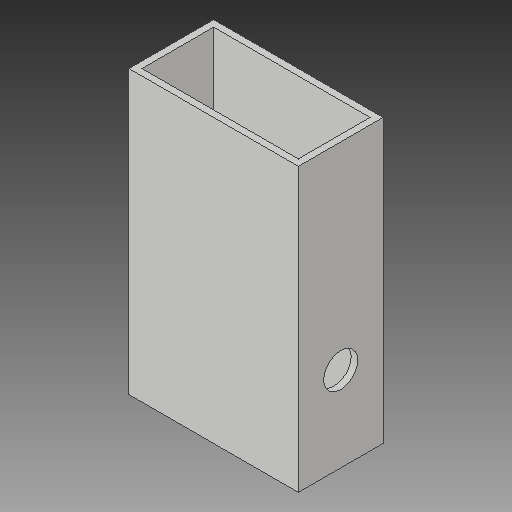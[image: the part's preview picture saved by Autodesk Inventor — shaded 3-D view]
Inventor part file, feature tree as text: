
AUTODESK INVENTOR PART (.ipt)
format: ipt  version: 2018 (Build 220112000, 112)  size: 103,424 bytes
history: native  units: mm
features: extrude x2, sketch x2, other x1
ambient origin geometry x8: Origin, YZ Plane, XZ Plane, XY Plane, X Axis, Y Axis, Z Axis, Center Point
bodies: Body1 (feature_tree)
feature tree (5):
  other  "ソリッド1"
  extrude  "押し出し1"  Depth=60.0mm
  extrude  "押し出し2"  Depth=30.0mm
  sketch  "スケッチ2"
  sketch  "スケッチ3"
